# Revit family: Sink-Kitchen-KOHLER-Whitehaven-K-6349
name_source: partatom
category: Plumbing Fixtures
revit_build: Autodesk Revit 2015 (Build: 20140606_1530(x64)
units: mm (PartAtom-declared; Revit-internal decimal feet)

## types (1)
- 0-White
    ADA Compliant = No
    Assembly Code = D2010400
    CW Connection = No
    Cold Water Inlet = Cold Water Inlet
    Date Modified = 01/10/2019
    Default Elevation = 36"
    Description = Self-Trimming Smart Divide 35-11/16 inch x 21-9/16 inch x 9-5/8 inch under-mount large/medium double-bowl kitchen sink with tall apron and Hayridge design
    Drain Included = No
    Finish = Kohler-Enameled_Cast_Iron-0-White
    HW Connection = No
    Height = 9 5/8"
    Hot Water Inlet = Hot Water Inlet
    Length = 35 11/16"
    Manufacturer = KOHLER Co.
    MasterFormat 1995 = 15410
    MasterFormat 2004 = 22.41.16
    Material = Enameled Cast Iron
    Model = K-6349-0
    Product Documentation Link = https://www.us.kohler.com
    Product Name = Whitehaven
    Product Page URL = http://www.us.kohler.com
    Type = 1
    URL = https://www.us.kohler.com
    Vent Connection = No
    Waste Connection = Yes
    Waste Water Outlet 1 = Waste Water Outlet 1
    Waste Water Outlet 2 = Waste Water Outlet 2
    WaterSense Certified = No
    Width = 21 9/16"

## geometry (parser evidence)
native form markers: Sweep x5
no freeform markers — native parametric forms only
